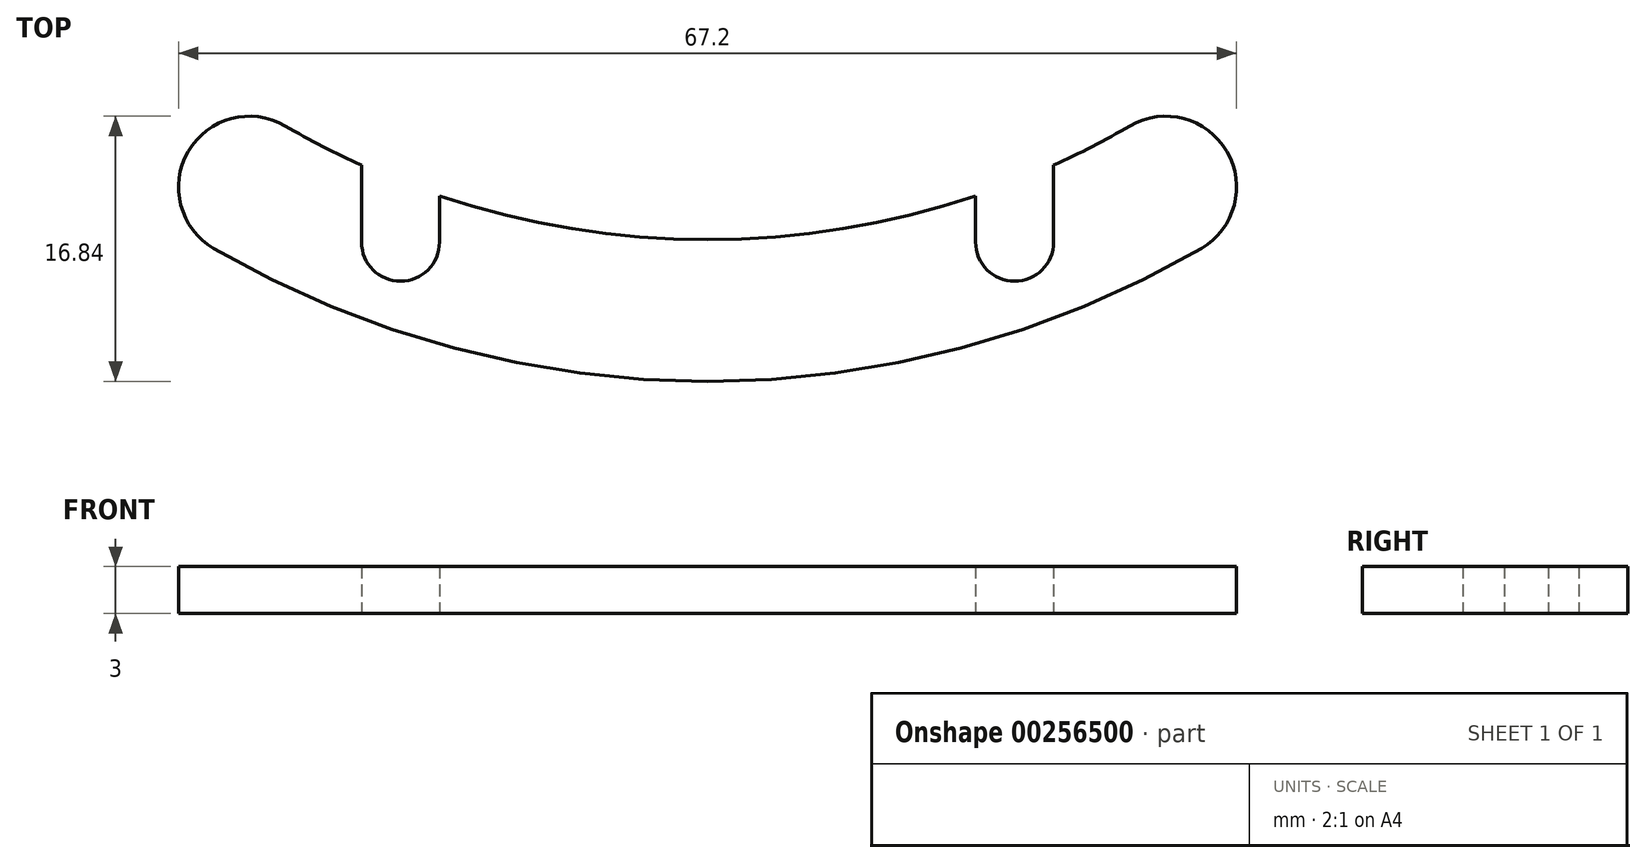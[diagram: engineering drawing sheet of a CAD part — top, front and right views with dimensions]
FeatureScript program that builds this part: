
annotation { "Feature Type Name" : "Feature", "Feature Type Description" : "" }
export const myFeature = defineFeature(function(context is Context, id is Id, definition is map)
    precondition{}
    {
        {
            var Q0;
            Q0=qCreatedBy(makeId("Top.planeOp"),FACE);
            var sketch = newSketch(context, id + "F0", { "sketchPlane" : qUnion([Q0])});
            skArc(sketch, "E0", {"start": v(-8.95, -15.39) * mm, "mid": v(-8.15, -15.83) * mm, "end": v(-7.33, -16.22) * mm});
            skCircle(sketch, "E1", {"center": v(0, 0) * mm, "radius": 19 * mm, "construction": true});
            skArc(sketch, "E2", {"start": v(-10.45, -17.98) * mm, "mid": v(0, -20.8) * mm, "end": v(10.45, -17.98) * mm});
            skArc(sketch, "E3", {"start": v(-8.95, -15.39) * mm, "mid": v(-11, -15.93) * mm, "end": v(-10.45, -17.98) * mm});
            skArc(sketch, "E4", {"start": v(10.45, -17.98) * mm, "mid": v(11, -15.93) * mm, "end": v(8.95, -15.39) * mm});
            skArc(sketch, "E5", {"start": v(-7.33, -17.85) * mm, "mid": v(-6.5, -18.68) * mm, "end": v(-5.68, -17.85) * mm});
            skArc(sketch, "E6", {"start": v(5.68, -17.85) * mm, "mid": v(6.5, -18.68) * mm, "end": v(7.33, -17.85) * mm});
            skLineSegment(sketch, "E7", {"start": v(-7.33, -17.85) * mm, "end": v(-7.33, -16.22) * mm});
            skLineSegment(sketch, "E8", {"start": v(-5.68, -17.85) * mm, "end": v(-5.68, -16.87) * mm});
            skLineSegment(sketch, "E9", {"start": v(5.68, -17.85) * mm, "end": v(5.68, -16.87) * mm});
            skLineSegment(sketch, "E10", {"start": v(7.33, -17.85) * mm, "end": v(7.33, -16.22) * mm});
            skArc(sketch, "E11.trimOffspring", {"start": v(-5.67, -16.87) * mm, "mid": v(0, -17.8) * mm, "end": v(5.67, -16.87) * mm});
            skArc(sketch, "E12.trimOffspring", {"start": v(7.33, -16.22) * mm, "mid": v(8.15, -15.83) * mm, "end": v(8.95, -15.39) * mm});
            skSolve(sketch);
        }
        {
            var Q0;
            Q0=makeQuery(id+"F0.imprint","IMPRINT",FACE,{"disambiguationData":[TD([[makeQuery(id+"F0.imprint","IMPRINT",EDGE,{"derivedFrom":sQuery(id+"F0.wireOp",EDGE,"E0")}),-1.0]])]});
            extrude(context, id + "F1", {"entities" : qUnion([Q0]), "depth" : 1 * mm});
        }
        {
            var Q0;
            Q0=makeQuery(id+"F1.opExtrude","SWEPT_BODY",BODY,{"disambiguationData":[OSD([sQuery(id+"F0.wireOp",EDGE,"E0"),sQuery(id+"F0.wireOp",EDGE,"E2"),sQuery(id+"F0.wireOp",EDGE,"E3"),sQuery(id+"F0.wireOp",EDGE,"E4"),sQuery(id+"F0.wireOp",EDGE,"E5"),sQuery(id+"F0.wireOp",EDGE,"E6"),sQuery(id+"F0.wireOp",EDGE,"E7"),sQuery(id+"F0.wireOp",EDGE,"E8"),sQuery(id+"F0.wireOp",EDGE,"E9"),sQuery(id+"F0.wireOp",EDGE,"E10"),sQuery(id+"F0.wireOp",EDGE,"E11.trimOffspring"),sQuery(id+"F0.wireOp",EDGE,"E12.trimOffspring")])]});
            var Q1;
            Q1=qCreatedBy(makeId("Origin.pointOp"),VERTEX);
            transform(context, id + "F2", {"entities" : qUnion([Q0]), "transformType" : TransformType.SCALE_UNIFORMLY, "scale" : 3, "makeCopy" : false, "scalePoint" : qUnion([Q1])});
        }
    });
